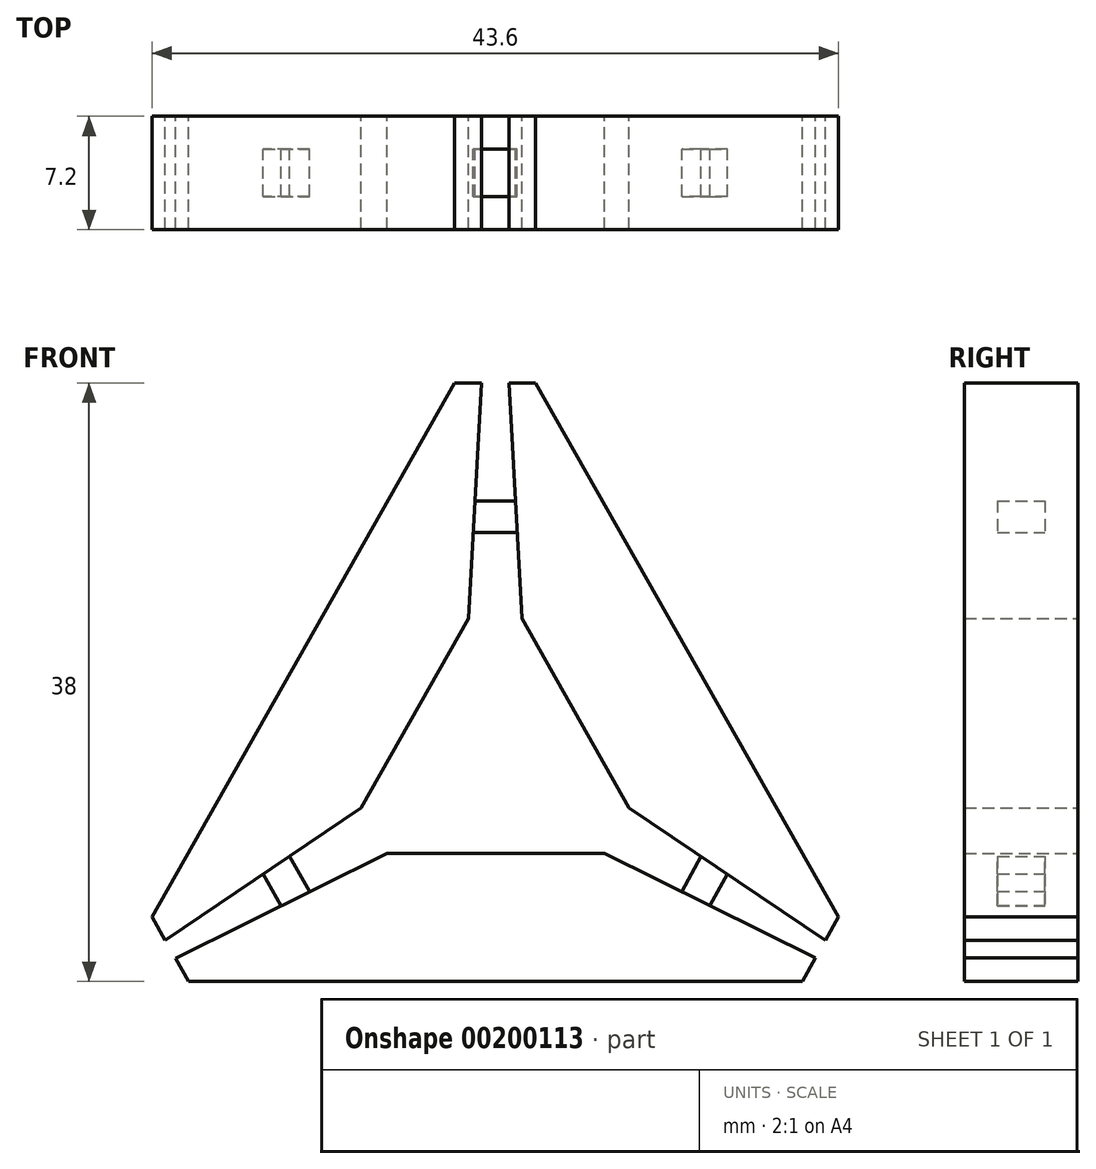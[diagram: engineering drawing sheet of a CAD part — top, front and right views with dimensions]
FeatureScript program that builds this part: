
annotation { "Feature Type Name" : "Feature", "Feature Type Description" : "" }
export const myFeature = defineFeature(function(context is Context, id is Id, definition is map)
    precondition{}
    {
        {
            var Q0;
            Q0=qCreatedBy(makeId("Front.planeOp"),FACE);
            var sketch = newSketch(context, id + "F0", { "sketchPlane" : qUnion([Q0])});
            skLineSegment(sketch, "E0", {"start": v(-6.76, 8.5) * mm, "end": v(-20.18, 1.84) * mm});
            skLineSegment(sketch, "E1", {"start": v(-20.18, 1.84) * mm, "end": v(-19.34, 0.37) * mm});
            skLineSegment(sketch, "E2", {"start": v(-19.34, 0.37) * mm, "end": v(19.64, 0.37) * mm});
            skLineSegment(sketch, "E3", {"start": v(19.64, 0.37) * mm, "end": v(20.47, 1.85) * mm});
            skLineSegment(sketch, "E4", {"start": v(20.47, 1.85) * mm, "end": v(7.06, 8.5) * mm});
            skLineSegment(sketch, "E5", {"start": v(7.06, 8.5) * mm, "end": v(-6.76, 8.5) * mm});
            skLineSegment(sketch, "E6", {"start": v(8.64, 11.39) * mm, "end": v(21.1, 2.97) * mm});
            skLineSegment(sketch, "E7", {"start": v(21.1, 2.97) * mm, "end": v(21.93, 4.46) * mm});
            skLineSegment(sketch, "E8", {"start": v(21.93, 4.46) * mm, "end": v(2.7, 38.37) * mm});
            skLineSegment(sketch, "E9", {"start": v(2.7, 38.37) * mm, "end": v(1, 38.37) * mm});
            skLineSegment(sketch, "E10", {"start": v(1, 38.37) * mm, "end": v(1.82, 23.4) * mm});
            skLineSegment(sketch, "E11", {"start": v(1.82, 23.4) * mm, "end": v(8.64, 11.39) * mm});
            skLineSegment(sketch, "E12", {"start": v(-8.38, 11.39) * mm, "end": v(-20.83, 2.98) * mm});
            skLineSegment(sketch, "E13", {"start": v(-20.83, 2.98) * mm, "end": v(-21.67, 4.46) * mm});
            skLineSegment(sketch, "E14", {"start": v(-21.67, 4.46) * mm, "end": v(-2.44, 38.37) * mm});
            skLineSegment(sketch, "E15", {"start": v(-2.44, 38.37) * mm, "end": v(-0.74, 38.37) * mm});
            skLineSegment(sketch, "E16", {"start": v(-0.74, 38.37) * mm, "end": v(-1.57, 23.4) * mm});
            skLineSegment(sketch, "E17", {"start": v(-1.57, 23.4) * mm, "end": v(-8.38, 11.39) * mm});
            skSolve(sketch);
        }
        {
            var Q0;
            Q0=makeQuery(id+"F0.imprint","IMPRINT",FACE,{"disambiguationData":[TD([[makeQuery(id+"F0.imprint","IMPRINT",EDGE,{"derivedFrom":sQuery(id+"F0.wireOp",EDGE,"E12")}),-1.0]])]});
            var Q1;
            Q1=makeQuery(id+"F0.imprint","IMPRINT",FACE,{"disambiguationData":[TD([[makeQuery(id+"F0.imprint","IMPRINT",EDGE,{"derivedFrom":sQuery(id+"F0.wireOp",EDGE,"E6")}),1.0]])]});
            var Q2;
            Q2=makeQuery(id+"F0.imprint","IMPRINT",FACE,{"disambiguationData":[TD([[makeQuery(id+"F0.imprint","IMPRINT",EDGE,{"derivedFrom":sQuery(id+"F0.wireOp",EDGE,"E0")}),1.0]])]});
            extrude(context, id + "F1", {"entities" : qUnion([Q0, Q1, Q2]), "endBound" : BoundingType.SYMMETRIC, "depth" : 7.2 * mm});
        }
        {
            var Q0;
            Q0=qCreatedBy(makeId("Front.planeOp"),FACE);
            var sketch = newSketch(context, id + "F2", { "sketchPlane" : qUnion([Q0])});
            skPoint(sketch, "E18.0", {"position": v(13.76, 5.18) * mm});
            skPoint(sketch, "E18.1", {"position": v(14.87, 7.18) * mm});
            skLineSegment(sketch, "E19", {"start": v(13.76, 5.18) * mm, "end": v(14.87, 7.18) * mm});
            skPoint(sketch, "E20.0", {"position": v(1.41, 30.88) * mm});
            skPoint(sketch, "E20.1", {"position": v(-1.16, 30.88) * mm});
            skPoint(sketch, "E21.0", {"position": v(-14.6, 7.18) * mm});
            skPoint(sketch, "E21.1", {"position": v(-13.47, 5.17) * mm});
            skLineSegment(sketch, "E22", {"start": v(-14.6, 7.18) * mm, "end": v(-13.47, 5.17) * mm});
            skLineSegment(sketch, "E23", {"start": v(-1.16, 30.88) * mm, "end": v(1.41, 30.88) * mm});
            skLineSegment(sketch, "E24", {"start": v(1.41, 30.88) * mm, "end": v(1.52, 28.88) * mm});
            skLineSegment(sketch, "E25", {"start": v(1.52, 28.88) * mm, "end": v(-1.26, 28.88) * mm});
            skLineSegment(sketch, "E26", {"start": v(-1.26, 28.88) * mm, "end": v(-1.16, 30.88) * mm});
            skLineSegment(sketch, "E27", {"start": v(14.87, 7.18) * mm, "end": v(13.2, 8.3) * mm});
            skLineSegment(sketch, "E28", {"start": v(13.2, 8.3) * mm, "end": v(11.98, 6.07) * mm});
            skLineSegment(sketch, "E29", {"start": v(11.98, 6.07) * mm, "end": v(13.76, 5.18) * mm});
            skLineSegment(sketch, "E30", {"start": v(-13.47, 5.17) * mm, "end": v(-11.67, 6.07) * mm});
            skLineSegment(sketch, "E31", {"start": v(-11.67, 6.07) * mm, "end": v(-12.94, 8.3) * mm});
            skLineSegment(sketch, "E32", {"start": v(-12.94, 8.3) * mm, "end": v(-14.6, 7.18) * mm});
            skSolve(sketch);
        }
        {
            var Q0;
            Q0=makeQuery(id+"F2.imprint","IMPRINT",FACE,{"disambiguationData":[TD([[makeQuery(id+"F2.imprint","IMPRINT",EDGE,{"derivedFrom":sQuery(id+"F2.wireOp",EDGE,"E23")}),-1.0]])]});
            var Q1;
            Q1=makeQuery(id+"F2.imprint","IMPRINT",FACE,{"disambiguationData":[TD([[makeQuery(id+"F2.imprint","IMPRINT",EDGE,{"derivedFrom":sQuery(id+"F2.wireOp",EDGE,"E22")}),1.0]])]});
            var Q2;
            Q2=makeQuery(id+"F2.imprint","IMPRINT",FACE,{"disambiguationData":[TD([[makeQuery(id+"F2.imprint","IMPRINT",EDGE,{"derivedFrom":sQuery(id+"F2.wireOp",EDGE,"E19")}),1.0]])]});
            extrude(context, id + "F3", {"entities" : qUnion([Q0, Q1, Q2]), "operationType" : NewBodyOperationType.ADD, "endBound" : BoundingType.SYMMETRIC, "depth" : 3 * mm});
        }
    });
